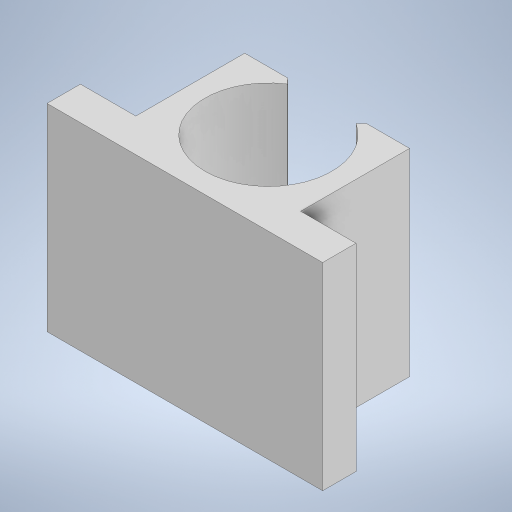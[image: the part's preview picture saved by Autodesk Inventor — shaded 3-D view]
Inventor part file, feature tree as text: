
AUTODESK INVENTOR PART (.ipt)
format: ipt  version: 2024 (Build 280153000, 153)  size: 221,696 bytes
history: native  units: mm
features: extrude x2, sketch x2
ambient origin geometry x8: Origin, YZ Plane, XZ Plane, XY Plane, X Axis, Y Axis, Z Axis, Center Point
bodies: Solid1 (feature_tree)
feature tree (4):
  extrude  "Extrusion1"  Depth=50.0mm TaperAngle=0.0deg
  extrude  "Extrusion2"  Depth=50.0mm
  sketch  "Sketch1"  dims[d0=0.0mm d1=32.1mm d2=12.0mm d3=12.0mm d4=50.0mm d5=0.0mm]
  sketch  "Sketch3"  dims[d9=2.0mm d10=2.0mm d11=0.0mm d12=50.0mm d13=0.0mm]
